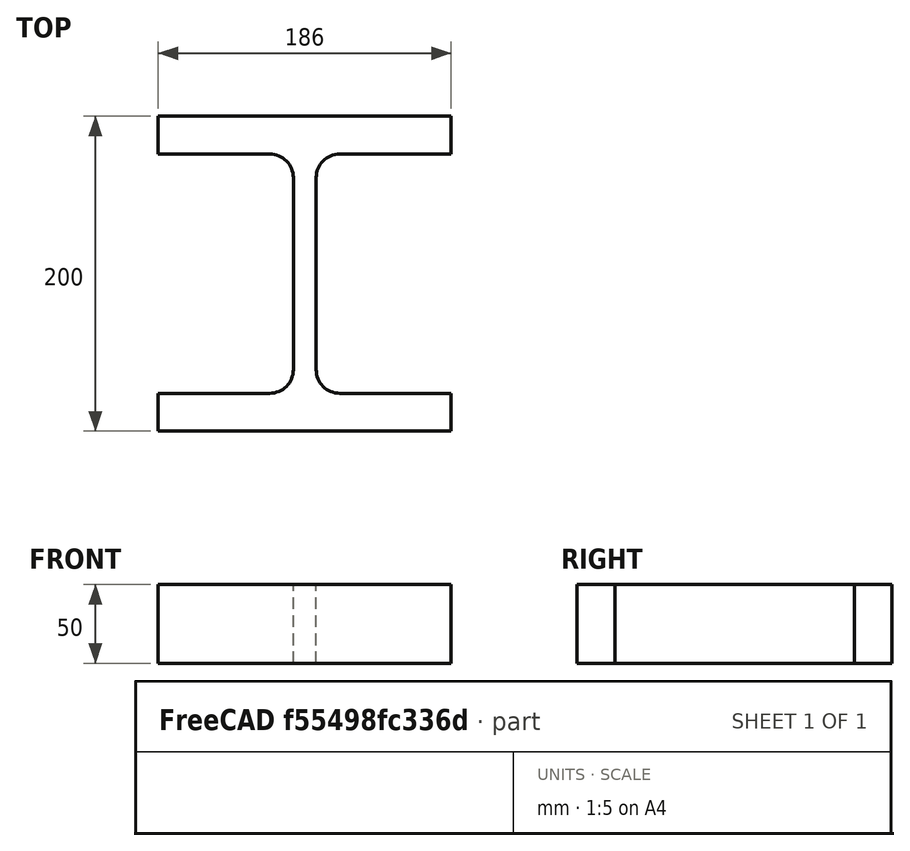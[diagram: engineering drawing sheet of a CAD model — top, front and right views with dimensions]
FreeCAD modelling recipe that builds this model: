
FCSTD DOCUMENT  (FreeCAD 0.15R4671 (Git))
Label: HE-M-Profile 180 DIN1025-4 S235JR
License: All rights reserved
LicenseURL: http://en.wikipedia.org/wiki/All_rights_reserved
objects: Sketcher::SketchObject×1, Part::Extrusion×1
note: 2 computed .brp shape members not serialized (recipe doc carries the construction recipe); baked Part::Feature solids carry a one-line shape summary decoded from their .brp

FEATURE [Sketcher::SketchObject] Sketch
  sketch-geometry (16):
    g0: LineSegment StartX=7.25 StartY=-61 StartZ=0 EndX=7.25 EndY=61 EndZ=0
    g1: LineSegment StartX=22.25 StartY=76 StartZ=0 EndX=93 EndY=76 EndZ=0
    g2: LineSegment StartX=93 StartY=76 StartZ=0 EndX=93 EndY=100 EndZ=0
    g3: LineSegment StartX=93 StartY=100 StartZ=0 EndX=-93 EndY=100 EndZ=0
    g4: LineSegment StartX=-93 StartY=100 StartZ=0 EndX=-93 EndY=76 EndZ=0
    g5: LineSegment StartX=-93 StartY=76 StartZ=0 EndX=-22.25 EndY=76 EndZ=0
    g6: LineSegment StartX=-7.25 StartY=61 StartZ=0 EndX=-7.25 EndY=-61 EndZ=0
    g7: LineSegment StartX=-22.25 StartY=-76 StartZ=0 EndX=-93 EndY=-76 EndZ=0
    g8: LineSegment StartX=-93 StartY=-76 StartZ=0 EndX=-93 EndY=-100 EndZ=0
    g9: LineSegment StartX=-93 StartY=-100 StartZ=0 EndX=93 EndY=-100 EndZ=0
    g10: LineSegment StartX=93 StartY=-100 StartZ=0 EndX=93 EndY=-76 EndZ=0
    g11: LineSegment StartX=93 StartY=-76 StartZ=0 EndX=22.25 EndY=-76 EndZ=0
    g12: ArcOfCircle CenterX=22.25 CenterY=61 CenterZ=0 NormalX=0 NormalY=0 NormalZ=1 Radius=15 StartAngle=1.5708 EndAngle=3.14159
    g13: ArcOfCircle CenterX=22.25 CenterY=-61 CenterZ=0 NormalX=0 NormalY=0 NormalZ=1 Radius=15 StartAngle=3.14159 EndAngle=4.71239
    g14: ArcOfCircle CenterX=-22.25 CenterY=61 CenterZ=0 NormalX=0 NormalY=0 NormalZ=1 Radius=15 StartAngle=0 EndAngle=1.5708
    g15: ArcOfCircle CenterX=-22.25 CenterY=-61 CenterZ=0 NormalX=0 NormalY=0 NormalZ=1 Radius=15 StartAngle=4.71239 EndAngle=6.28319
  constraints (42):
    c: Vertical(g0)
    c: Coincident(g2,g1)
    c: Vertical(g2)
    c: Coincident(g3,g2)
    c: Coincident(g4,g3)
    c: Vertical(g4)
    c: Coincident(g5,g4)
    c: Horizontal(g5)
    c: Vertical(g6)
    c: Horizontal(g7)
    c: Coincident(g8,g7)
    c: Vertical(g8)
    c: Coincident(g9,g8)
    c: Horizontal(g9)
    c: Coincident(g10,g9)
    c: Vertical(g10)
    c: Coincident(g11,g10)
    c: Horizontal(g11)
    c: Tangent(g1,g12) = 1.5708
    c: Tangent(g0,g12) = 1.5708
    c: Tangent(g0,g13) = 1.5708
    c: Tangent(g11,g13) = 1.5708
    c: Tangent(g5,g14) = 1.5708
    c: Tangent(g6,g14) = 1.5708
    c: Tangent(g6,g15) = 1.5708
    c: Tangent(g7,g15) = 1.5708
    c: Equal(g3,g9)
    c: Equal(g2,g4)
    c: Equal(g4,g8)
    c: Equal(g8,g10)
    c: Equal(g12,g14)
    c: Equal(g14,g15)
    c: Equal(g15,g13)
    c: Symmetric(g2,g3,g-2)
    c: Symmetric(g9,g8,g-2)
    c: Symmetric(g0,g6,g-2)
    c: Symmetric(g2,g9,g-1)
    c: DistanceY(g2,g9) = -200
    c: DistanceX(g3) = -186
    c: DistanceX(g0,g6) = -14.5
    c: DistanceY(g2) = 24
    c: Radius(g12) = 15
FEATURE [Part::Extrusion] Extrude  label="HE-M-Profile 180 DIN1025-4 S235JR"
  Base = -> Sketch
  Dir = (0,0,50)
  Solid = true
